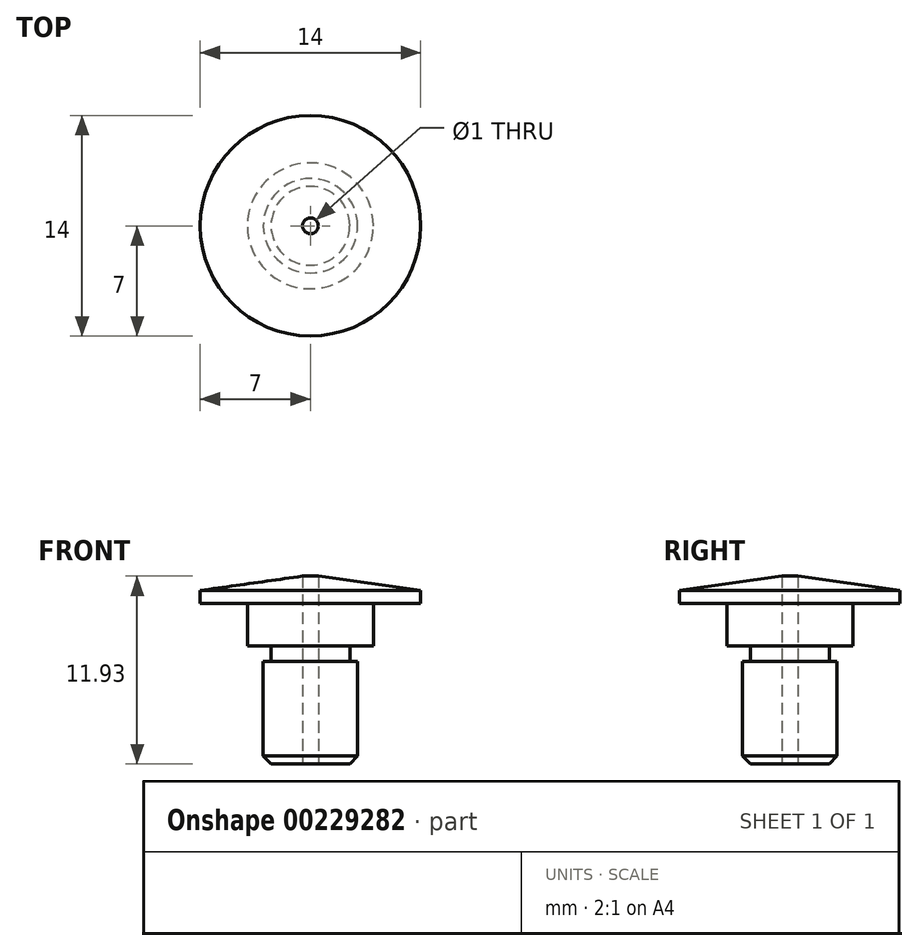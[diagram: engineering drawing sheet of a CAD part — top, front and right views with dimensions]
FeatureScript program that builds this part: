
annotation { "Feature Type Name" : "Feature", "Feature Type Description" : "" }
export const myFeature = defineFeature(function(context is Context, id is Id, definition is map)
    precondition{}
    {
        {
            var Q0;
            Q0=qCreatedBy(makeId("Front.planeOp"),FACE);
            var sketch = newSketch(context, id + "F0", { "sketchPlane" : qUnion([Q0])});
            skLineSegment(sketch, "E0", {"start": v(0, 12) * mm, "end": v(-7, 11.02) * mm});
            skLineSegment(sketch, "E1", {"start": v(-7, 11.02) * mm, "end": v(-7, 10.2) * mm});
            skLineSegment(sketch, "E2", {"start": v(-7, 10.2) * mm, "end": v(-4, 10.2) * mm});
            skLineSegment(sketch, "E3", {"start": v(-4, 10.2) * mm, "end": v(-4, 7.5) * mm});
            skLineSegment(sketch, "E4", {"start": v(-4, 7.5) * mm, "end": v(-2.5, 7.5) * mm});
            skLineSegment(sketch, "E5", {"start": v(-2.5, 7.5) * mm, "end": v(-2.5, 6.5) * mm});
            skLineSegment(sketch, "E6", {"start": v(-2.5, 6.5) * mm, "end": v(-3, 6.5) * mm});
            skLineSegment(sketch, "E7", {"start": v(-3, 6.5) * mm, "end": v(-3, 0.5) * mm});
            skLineSegment(sketch, "E8", {"start": v(-3, 0.5) * mm, "end": v(-2.5, 0) * mm});
            skLineSegment(sketch, "E9", {"start": v(-2.5, 0) * mm, "end": v(0, 0) * mm});
            skLineSegment(sketch, "E10", {"start": v(0, 0) * mm, "end": v(0, 12) * mm});
            skSolve(sketch);
        }
        {
            var Q0;
            Q0=makeQuery(id+"F0.imprint","IMPRINT",FACE,{"disambiguationData":[TD([[makeQuery(id+"F0.imprint","IMPRINT",EDGE,{"derivedFrom":sQuery(id+"F0.wireOp",EDGE,"E0")}),1.0]])]});
            var Q1;
            Q1=sQuery(id+"F0.wireOp",EDGE,"E10");
            revolve(context, id + "F1", {"entities" : qUnion([Q0]), "axis" : qUnion([Q1]), "revolveType" : RevolveType.FULL});
        }
        {
            var Q0;
            Q0=qCreatedBy(makeId("Top.planeOp"),FACE);
            var sketch = newSketch(context, id + "F2", { "sketchPlane" : qUnion([Q0])});
            skCircle(sketch, "E11", {"center": v(0, 0) * mm, "radius": 0.5 * mm});
            skSolve(sketch);
        }
        {
            var Q0;
            Q0=makeQuery(id+"F2.imprint","IMPRINT",FACE,{"disambiguationData":[TD([[makeQuery(id+"F2.imprint","IMPRINT",EDGE,{"derivedFrom":sQuery(id+"F2.wireOp",EDGE,"E11")}),1.0]])]});
            extrude(context, id + "F3", {"entities" : qUnion([Q0]), "operationType" : NewBodyOperationType.REMOVE, "depth" : 25 * mm});
        }
    });
